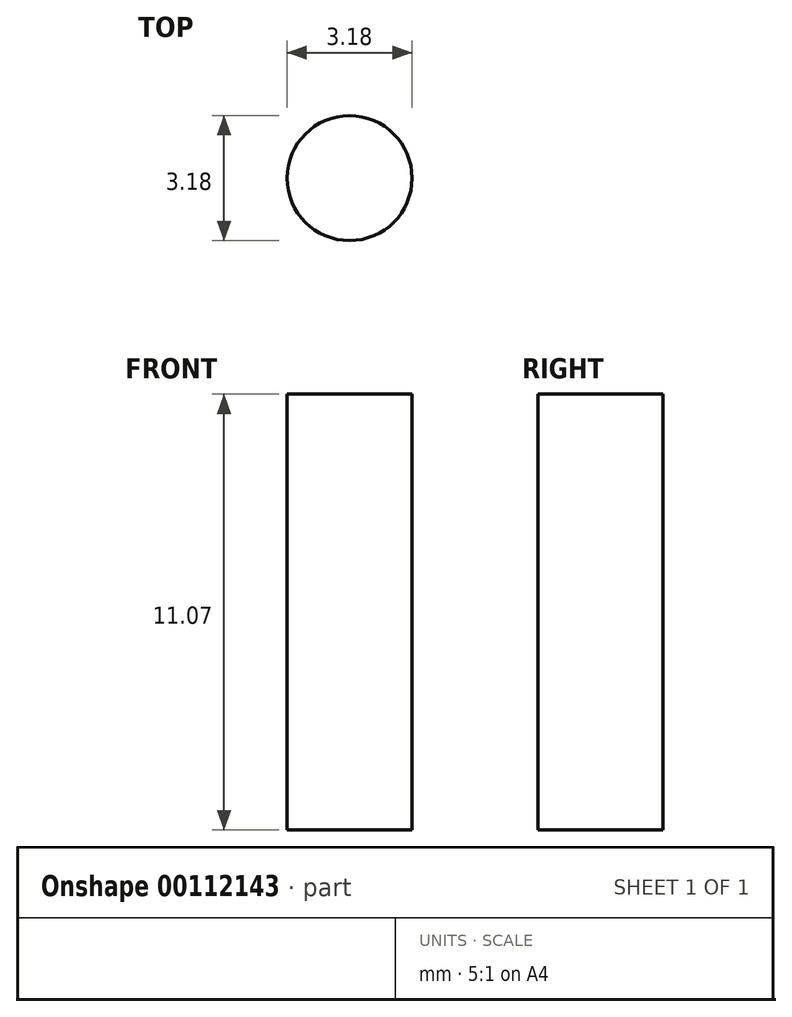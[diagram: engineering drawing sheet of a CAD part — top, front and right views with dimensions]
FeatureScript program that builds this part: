
annotation { "Feature Type Name" : "Feature", "Feature Type Description" : "" }
export const myFeature = defineFeature(function(context is Context, id is Id, definition is map)
    precondition{}
    {
        {
            var Q0;
            Q0=qCreatedBy(makeId("Top.planeOp"),FACE);
            var sketch = newSketch(context, id + "F0", { "sketchPlane" : qUnion([Q0])});
            skCircle(sketch, "E0", {"center": v(0, 0) * mm, "radius": 1.59 * mm});
            skSolve(sketch);
        }
        {
            var Q0;
            Q0=makeQuery(id+"F0.imprint","IMPRINT",FACE,{"disambiguationData":[TD([[makeQuery(id+"F0.imprint","IMPRINT",EDGE,{"derivedFrom":sQuery(id+"F0.wireOp",EDGE,"E0")}),1.0]])]});
            extrude(context, id + "F1", {"entities" : qUnion([Q0]), "depth" : 11.07 * mm});
        }
    });
